AUTODESK INVENTOR PART (.ipt)
format: ipt  version: 2017 (Build 210142000, 142)  size: 245,760 bytes
history: native  units: in
note: dims shown in document units (in); Inventor stores cm internally (conversion verified against a paired STEP export)
features: sketch x8, other x7, hole x6, projected_geometry x3, extrude x1
ambient origin geometry x8: Origin, YZ Plane, XZ Plane, XY Plane, X Axis, Y Axis, Z Axis, Center Point
bodies: Solid1 (feature_tree)
feature tree (25):
  extrude  "PDU bottom"  Depth=16.45in
  other  "Interface circuit board sketch"
  other  "5V monitor psu sketch"
  hole  "Inteface circuit board holes "  [1 undecoded]
  hole  "5V monitor psu holes"  [1 undecoded]
  other  "thermostat sketch"
  hole  "thermostat holes"  [1 undecoded]
  other  "wrlen"
  hole  "wrlen holes"  [1 undecoded]
  other  "arduino"
  other  "power plugs"
  hole  "arduino holes"  [1 undecoded]
  other  "snap relay"
  hole  "snap relay holes"  [1 undecoded]
  sketch  "Sketch21"  dims[d104=0.1339in d105=0.2362in d106=0.248in d107=0.0787in d108=90.0deg d109=0.315in d110=0.8108in d128=0.375in d129=0.375in d130=4.139in d131=5.326in d134=0.5in d135=0.5in d138=0.5in d139=0.5in d140=0.455in d141=7.022in d149=0.134in d150=0.75in d151=0.248in d152=0.25in d153=90.0deg d154=1.0in d155=0.8108in d156=1.909in d157=1.909in d158=1.959in d159=1.742in d165=0.433in d168=4.07in d169=2.73in d170=3.0in d172=1.345in d173=9.17in d174=1.124in d175=3.0in d176=14.668in d177=2.7in d178=2.1in d179=0.985in d180=0.6in d181=0.1in d182=0.1in d183=0.1in d184=0.3in d185=1.4in d186=0.114in d187=0.75in d188=0.217in d189=0.25in d190=90.0deg d191=1.0in d192=0.8108in d193=5.4in d194=2.1in d195=0.7in d196=0.95in d197=5.2in d200=0.134in d201=0.75in d202=0.248in d203=0.25in d204=90.0deg d205=1.0in d206=0.8108in d207=1.97in d208=1.97in d209=5.2in d210=8.5in d211=2.0in d212=3.0in d213=13.909in d214=13.909in d215=0.625in d216=0.625in d217=3.25in d218=3.25in d219=0.375in d220=0.375in]
  sketch  "Sketch1"  dims[d0=19.37in d1=16.45in]
  sketch  "Sketch7"  dims[d2=0.065in d3=0.0in d4=6.25in]
  projected_geometry  "Projected Loop3"
  sketch  "Sketch9"  dims[d5=1.75in d7=0.7874in d9=3.5in d10=0.7874in d12=3.5in]
  projected_geometry  "Projected Loop5"
  sketch  "Sketch11"  dims[d22=13.428in d25=10.869in]
  projected_geometry  "Projected Loop6"
  sketch  "Sketch15"  dims[d80=0.134in d81=0.2362in d82=0.248in d83=0.0787in d84=90.0deg d85=0.315in d86=0.8108in]
  sketch  "Sketch18"  dims[d94=0.134in d95=0.2362in d96=0.248in d97=0.0787in d98=90.0deg d99=0.315in d100=0.8108in d101=6.352in]
  sketch  "Sketch20"  dims[d102=14.3588in d103=0.938in]
note: 6 required parameter values undecoded (feature->parameter linkage not recoverable at this tier; creation-order binding heuristic only, values carry confidence <= 0.55)
